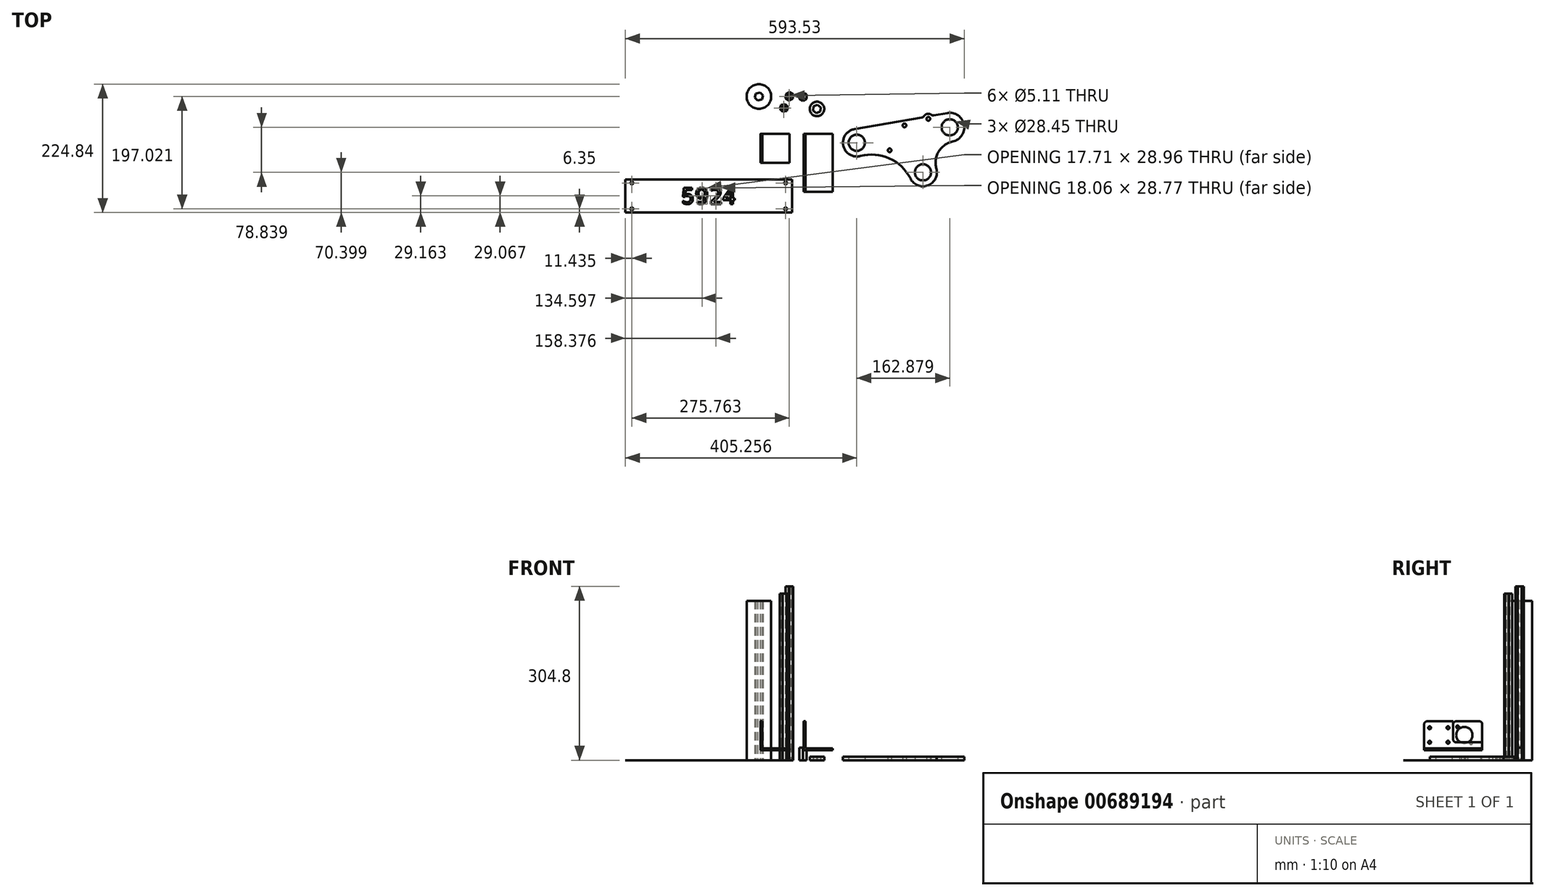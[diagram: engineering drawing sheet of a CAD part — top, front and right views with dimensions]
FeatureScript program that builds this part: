
annotation { "Feature Type Name" : "Feature", "Feature Type Description" : "" }
export const myFeature = defineFeature(function(context is Context, id is Id, definition is map)
    precondition{}
    {
        {
            var Q0;
            Q0=qCreatedBy(makeId("Front.planeOp"),FACE);
            var sketch = newSketch(context, id + "F0", { "sketchPlane" : qUnion([Q0])});
            skLineSegment(sketch, "E0", {"start": v(-58.96, 68.21) * mm, "end": v(-58.96, 17.41) * mm});
            skLineSegment(sketch, "E1", {"start": v(-58.96, 17.41) * mm, "end": v(-8.16, 17.41) * mm});
            skLineSegment(sketch, "E2", {"start": v(-8.16, 17.41) * mm, "end": v(-8.16, 20.59) * mm});
            skLineSegment(sketch, "E3", {"start": v(-8.16, 20.59) * mm, "end": v(-55.78, 20.59) * mm});
            skLineSegment(sketch, "E4", {"start": v(-55.78, 20.59) * mm, "end": v(-55.78, 68.21) * mm});
            skLineSegment(sketch, "E5", {"start": v(-55.78, 68.21) * mm, "end": v(-58.96, 68.21) * mm});
            skLineSegment(sketch, "E6", {"start": v(16.98, 68.21) * mm, "end": v(16.98, 17.41) * mm});
            skLineSegment(sketch, "E7", {"start": v(16.98, 17.41) * mm, "end": v(67.78, 17.41) * mm});
            skLineSegment(sketch, "E8", {"start": v(67.78, 17.41) * mm, "end": v(67.78, 20.59) * mm});
            skLineSegment(sketch, "E9", {"start": v(67.78, 20.59) * mm, "end": v(20.15, 20.59) * mm});
            skLineSegment(sketch, "E10", {"start": v(20.15, 20.59) * mm, "end": v(20.15, 68.21) * mm});
            skLineSegment(sketch, "E11", {"start": v(20.15, 68.21) * mm, "end": v(16.98, 68.21) * mm});
            skSolve(sketch);
        }
        {
            var Q0;
            Q0=makeQuery(id+"F0.imprint","IMPRINT",FACE,{"disambiguationData":[TD([[makeQuery(id+"F0.imprint","IMPRINT",EDGE,{"derivedFrom":sQuery(id+"F0.wireOp",EDGE,"E0")}),1.0]])]});
            extrude(context, id + "F1", {"entities" : qUnion([Q0]), "depth" : 50.8 * mm, "offsetDistance" : 25.4 * mm});
        }
        {
            var Q0;
            Q0=makeQuery(id+"F0.imprint","IMPRINT",FACE,{"disambiguationData":[TD([[makeQuery(id+"F0.imprint","IMPRINT",EDGE,{"derivedFrom":sQuery(id+"F0.wireOp",EDGE,"E6")}),1.0]])]});
            extrude(context, id + "F2", {"entities" : qUnion([Q0]), "depth" : 101.6 * mm, "offsetDistance" : 25.4 * mm});
        }
        {
            var Q0;
            Q0=makeQuery(id+"F1.opExtrude","SWEPT_FACE",FACE,{"disambiguationData":[OSD([sQuery(id+"F0.wireOp",EDGE,"E0")])]});
            var sketch = newSketch(context, id + "F3", { "sketchPlane" : qUnion([Q0])});
            skLineSegment(sketch, "E12.0.0", {"start": v(0, 68.21) * mm, "end": v(0, 17.41) * mm, "construction": true});
            skLineSegment(sketch, "E12.0.1", {"start": v(0, 17.41) * mm, "end": v(50.8, 17.41) * mm, "construction": true});
            skLineSegment(sketch, "E12.0.2", {"start": v(50.8, 17.41) * mm, "end": v(50.8, 68.21) * mm, "construction": true});
            skLineSegment(sketch, "E12.0.3", {"start": v(50.8, 68.21) * mm, "end": v(0, 68.21) * mm, "construction": true});
            skCircle(sketch, "E13", {"center": v(31.35, 44.08) * mm, "radius": 14.29 * mm});
            skCircle(sketch, "E14", {"center": v(31.35, 44.08) * mm, "radius": 15.56 * mm, "construction": true});
            skCircle(sketch, "E15", {"center": v(43.2, 58.26) * mm, "radius": 2.41 * mm});
            skCircle(sketch, "E16", {"center": v(19.5, 29.9) * mm, "radius": 2.41 * mm});
            skLineSegment(sketch, "E17", {"start": v(19.5, 29.9) * mm, "end": v(43.2, 58.26) * mm, "construction": true});
            skSolve(sketch);
        }
        {
            var Q0;
            Q0 = qSketchRegion(id + "F3", true);
            var Q1;
            Q1=makeQuery(id+"F1.opExtrude","SWEPT_FACE",FACE,{"disambiguationData":[OSD([sQuery(id+"F0.wireOp",EDGE,"E4")])]});
            extrude(context, id + "F4", {"entities" : qUnion([Q0]), "operationType" : NewBodyOperationType.REMOVE, "endBound" : BoundingType.UP_TO_SURFACE, "oppositeDirection" : true, "depth" : 25.4 * mm, "endBoundEntityFace" : qUnion([Q1]), "offsetDistance" : 25.4 * mm});
        }
        {
            var Q0;
            Q0=makeQuery(id+"F1.opExtrude","CAP_EDGE",EDGE,{"disambiguationData":[OSD([sQuery(id+"F0.wireOp",EDGE,"E5")])],"isStart":false});
            var Q1;
            Q1=makeQuery(id+"F1.opExtrude","CAP_EDGE",EDGE,{"disambiguationData":[OSD([sQuery(id+"F0.wireOp",EDGE,"E5")])],"isStart":true});
            fillet(context, id + "F5", {"entities" : qUnion([Q0, Q1]), "radius" : 5.08 * mm, "tangentPropagation" : true, "allowEdgeOverflow" : false});
        }
        {
            var Q0;
            Q0=makeQuery(id+"F2.opExtrude","SWEPT_FACE",FACE,{"disambiguationData":[OSD([sQuery(id+"F0.wireOp",EDGE,"E10")])]});
            var sketch = newSketch(context, id + "F6", { "sketchPlane" : qUnion([Q0])});
            skLineSegment(sketch, "E18.0.0", {"start": v(0, 20.59) * mm, "end": v(0, 68.21) * mm, "construction": true});
            skLineSegment(sketch, "E18.0.1", {"start": v(0, 68.21) * mm, "end": v(-101.6, 68.21) * mm, "construction": true});
            skLineSegment(sketch, "E18.0.2", {"start": v(-101.6, 68.21) * mm, "end": v(-101.6, 20.59) * mm, "construction": true});
            skLineSegment(sketch, "E18.0.3", {"start": v(-101.6, 20.59) * mm, "end": v(0, 20.59) * mm, "construction": true});
            skLineSegment(sketch, "E19.bottom", {"start": v(-92.08, 56.78) * mm, "end": v(-59.94, 56.78) * mm, "construction": true});
            skLineSegment(sketch, "E19.top", {"start": v(-92.08, 31.38) * mm, "end": v(-59.94, 31.38) * mm, "construction": true});
            skLineSegment(sketch, "E19.left", {"start": v(-92.08, 56.78) * mm, "end": v(-92.08, 31.38) * mm, "construction": true});
            skLineSegment(sketch, "E19.right", {"start": v(-59.94, 56.78) * mm, "end": v(-59.94, 31.38) * mm, "construction": true});
            skPoint(sketch, "E19.middle", {"position": v(-76, 44.08) * mm});
            skCircle(sketch, "E20", {"center": v(-92.08, 56.78) * mm, "radius": 2.55 * mm});
            skCircle(sketch, "E21", {"center": v(-92.08, 31.38) * mm, "radius": 2.55 * mm});
            skCircle(sketch, "E22", {"center": v(-59.94, 31.38) * mm, "radius": 2.55 * mm});
            skCircle(sketch, "E23", {"center": v(-59.94, 56.78) * mm, "radius": 2.55 * mm});
            skLineSegment(sketch, "E24.0", {"start": v(-101.6, 17.41) * mm, "end": v(0, 17.41) * mm, "construction": true});
            skLineSegment(sketch, "E25.bottom", {"start": v(0, 68.21) * mm, "end": v(-50.8, 68.21) * mm});
            skLineSegment(sketch, "E25.top", {"start": v(0, 31.38) * mm, "end": v(-50.8, 31.38) * mm});
            skLineSegment(sketch, "E25.left", {"start": v(0, 68.21) * mm, "end": v(0, 31.38) * mm});
            skLineSegment(sketch, "E25.right", {"start": v(-50.8, 68.21) * mm, "end": v(-50.8, 31.38) * mm});
            skSolve(sketch);
        }
        {
            var Q0;
            Q0 = qSketchRegion(id + "F6", true);
            var Q1;
            Q1=makeQuery(id+"F2.opExtrude","SWEPT_FACE",FACE,{"disambiguationData":[OSD([sQuery(id+"F0.wireOp",EDGE,"E6")])]});
            extrude(context, id + "F7", {"entities" : qUnion([Q0]), "operationType" : NewBodyOperationType.REMOVE, "endBound" : BoundingType.UP_TO_SURFACE, "oppositeDirection" : true, "depth" : 25.4 * mm, "endBoundEntityFace" : qUnion([Q1]), "offsetDistance" : 25.4 * mm});
        }
        {
            var Q0;
            Q0=makeQuery(id+"F7.boolean.opBoolean","COPY",EDGE,{"derivedFrom":makeQuery(id+"F7.opExtrude","SWEPT_EDGE",EDGE,{"disambiguationData":[OSD([sQuery(id+"F6.wireOp",EDGE,"E25.top"),sQuery(id+"F6.wireOp",EDGE,"E25.right")])]})});
            var Q1;
            Q1=makeQuery(id+"F7.boolean.opBoolean","COPY",EDGE,{"derivedFrom":makeQuery(id+"F7.opExtrude","SWEPT_EDGE",EDGE,{"disambiguationData":[OSD([sQuery(id+"F0.wireOp",EDGE,"E10"),sQuery(id+"F0.wireOp",EDGE,"E11"),sQuery(id+"F6.wireOp",EDGE,"E25.bottom"),sQuery(id+"F6.wireOp",EDGE,"E25.right")])]})});
            var Q2;
            Q2=makeQuery(id+"F2.opExtrude","CAP_EDGE",EDGE,{"disambiguationData":[OSD([sQuery(id+"F0.wireOp",EDGE,"E11")])],"isStart":false});
            var Q3;
            Q3=makeQuery(id+"F7.boolean.opBoolean","COPY",EDGE,{"derivedFrom":makeQuery(id+"F7.opExtrude","SWEPT_EDGE",EDGE,{"disambiguationData":[OSD([sQuery(id+"F0.wireOp",EDGE,"E10"),sQuery(id+"F6.wireOp",EDGE,"E25.top"),sQuery(id+"F6.wireOp",EDGE,"E25.left")])]})});
            fillet(context, id + "F8", {"entities" : qUnion([Q0, Q1, Q2, Q3]), "radius" : 5.08 * mm, "tangentPropagation" : true, "allowEdgeOverflow" : false});
        }
        {
            var Q0;
            Q0=qCreatedBy(makeId("Top.planeOp"),FACE);
            var sketch = newSketch(context, id + "F9", { "sketchPlane" : qUnion([Q0])});
            skCircle(sketch, "E26", {"center": v(-61.67, 65.53) * mm, "radius": 21.59 * mm});
            skCircle(sketch, "E27.cCircle", {"center": v(-61.67, 65.53) * mm, "radius": 6.35 * mm, "construction": true});
            skLineSegment(sketch, "E27.0", {"start": v(-56.54, 60.29) * mm, "end": v(-63.65, 58.47) * mm});
            skLineSegment(sketch, "E27.1", {"start": v(-63.65, 58.47) * mm, "end": v(-68.77, 63.71) * mm});
            skLineSegment(sketch, "E27.2", {"start": v(-68.77, 63.71) * mm, "end": v(-66.8, 70.77) * mm});
            skLineSegment(sketch, "E27.3", {"start": v(-66.8, 70.77) * mm, "end": v(-59.7, 72.59) * mm});
            skLineSegment(sketch, "E27.4", {"start": v(-59.7, 72.59) * mm, "end": v(-54.57, 67.35) * mm});
            skLineSegment(sketch, "E27.5", {"start": v(-54.57, 67.35) * mm, "end": v(-56.54, 60.29) * mm});
            skPoint(sketch, "E27.0.midPoint", {"position": v(-60.1, 59.38) * mm});
            skSolve(sketch);
        }
        {
            var Q0;
            Q0=makeQuery(id+"F9.imprint","IMPRINT",FACE,{"disambiguationData":[TD([[makeQuery(id+"F9.imprint","IMPRINT",EDGE,{"derivedFrom":sQuery(id+"F9.wireOp",EDGE,"E26")}),1.0]])]});
            extrude(context, id + "F10", {"entities" : qUnion([Q0]), "depth" : 279.4 * mm, "offsetDistance" : 25.4 * mm});
        }
        {
            var Q0;
            Q0=qCreatedBy(makeId("Top.planeOp"),FACE);
            var sketch = newSketch(context, id + "F11", { "sketchPlane" : qUnion([Q0])});
            skCircle(sketch, "E28", {"center": v(-8.38, 65.65) * mm, "radius": 2.55 * mm});
            skCircle(sketch, "E29.cCircle", {"center": v(-8.38, 65.65) * mm, "radius": 6.35 * mm, "construction": true});
            skLineSegment(sketch, "E29.0", {"start": v(-2.1, 61.88) * mm, "end": v(-8.5, 58.32) * mm});
            skLineSegment(sketch, "E29.1", {"start": v(-8.5, 58.32) * mm, "end": v(-14.8, 62.1) * mm});
            skLineSegment(sketch, "E29.2", {"start": v(-14.8, 62.1) * mm, "end": v(-14.67, 69.42) * mm});
            skLineSegment(sketch, "E29.3", {"start": v(-14.67, 69.42) * mm, "end": v(-8.26, 72.98) * mm});
            skLineSegment(sketch, "E29.4", {"start": v(-8.26, 72.98) * mm, "end": v(-1.97, 69.21) * mm});
            skLineSegment(sketch, "E29.5", {"start": v(-1.97, 69.21) * mm, "end": v(-2.1, 61.88) * mm});
            skPoint(sketch, "E29.0.midPoint", {"position": v(-5.3, 60.1) * mm});
            skSolve(sketch);
        }
        {
            var Q0;
            Q0=makeQuery(id+"F11.imprint","IMPRINT",FACE,{"disambiguationData":[TD([[makeQuery(id+"F11.imprint","IMPRINT",EDGE,{"derivedFrom":sQuery(id+"F11.wireOp",EDGE,"E28")}),-1.0]])]});
            extrude(context, id + "F12", {"entities" : qUnion([Q0]), "depth" : 304.8 * mm, "offsetDistance" : 25.4 * mm});
        }
        {
            var Q0;
            Q0=qCreatedBy(makeId("Top.planeOp"),FACE);
            var sketch = newSketch(context, id + "F13", { "sketchPlane" : qUnion([Q0])});
            skCircle(sketch, "E30.cCircle", {"center": v(15.3, 65.5) * mm, "radius": 6.35 * mm, "construction": true});
            skLineSegment(sketch, "E30.0", {"start": v(21.75, 62) * mm, "end": v(15.5, 58.17) * mm});
            skLineSegment(sketch, "E30.1", {"start": v(15.5, 58.17) * mm, "end": v(9.05, 61.67) * mm});
            skLineSegment(sketch, "E30.2", {"start": v(9.05, 61.67) * mm, "end": v(8.86, 69) * mm});
            skLineSegment(sketch, "E30.3", {"start": v(8.86, 69) * mm, "end": v(15.12, 72.83) * mm});
            skLineSegment(sketch, "E30.4", {"start": v(15.12, 72.83) * mm, "end": v(21.56, 69.32) * mm});
            skLineSegment(sketch, "E30.5", {"start": v(21.56, 69.32) * mm, "end": v(21.75, 62) * mm});
            skPoint(sketch, "E30.0.midPoint", {"position": v(18.62, 60.08) * mm});
            skSolve(sketch);
        }
        {
            var Q0;
            Q0=makeQuery(id+"F13.imprint","IMPRINT",FACE,{"disambiguationData":[TD([[makeQuery(id+"F13.imprint","IMPRINT",EDGE,{"derivedFrom":sQuery(id+"F13.wireOp",EDGE,"E30.0")}),-1.0]])]});
            extrude(context, id + "F14", {"entities" : qUnion([Q0]), "depth" : 22.22 * mm, "offsetDistance" : 25.4 * mm});
        }
        {
            var Q0;
            Q0=qCreatedBy(makeId("Top.planeOp"),FACE);
            var sketch = newSketch(context, id + "F15", { "sketchPlane" : qUnion([Q0])});
            skCircle(sketch, "E31", {"center": v(40.06, 43.79) * mm, "radius": 12.7 * mm});
            skCircle(sketch, "E32.cCircle", {"center": v(40.06, 43.79) * mm, "radius": 6.35 * mm, "construction": true});
            skLineSegment(sketch, "E32.0", {"start": v(45.92, 39.38) * mm, "end": v(39.17, 36.51) * mm});
            skLineSegment(sketch, "E32.1", {"start": v(39.17, 36.51) * mm, "end": v(33.31, 40.92) * mm});
            skLineSegment(sketch, "E32.2", {"start": v(33.31, 40.92) * mm, "end": v(34.2, 48.2) * mm});
            skLineSegment(sketch, "E32.3", {"start": v(34.2, 48.2) * mm, "end": v(40.95, 51.07) * mm});
            skLineSegment(sketch, "E32.4", {"start": v(40.95, 51.07) * mm, "end": v(46.8, 46.66) * mm});
            skLineSegment(sketch, "E32.5", {"start": v(46.8, 46.66) * mm, "end": v(45.92, 39.38) * mm});
            skPoint(sketch, "E32.0.midPoint", {"position": v(42.54, 37.95) * mm});
            skSolve(sketch);
        }
        {
            var Q0;
            Q0=makeQuery(id+"F15.imprint","IMPRINT",FACE,{"disambiguationData":[TD([[makeQuery(id+"F15.imprint","IMPRINT",EDGE,{"derivedFrom":sQuery(id+"F15.wireOp",EDGE,"E31")}),1.0]])]});
            extrude(context, id + "F16", {"entities" : qUnion([Q0]), "depth" : 6.35 * mm, "offsetDistance" : 25.4 * mm});
        }
        {
            var Q0;
            Q0=qCreatedBy(makeId("Top.planeOp"),FACE);
            var sketch = newSketch(context, id + "F17", { "sketchPlane" : qUnion([Q0])});
            skCircle(sketch, "E33", {"center": v(225.6, -67.32) * mm, "radius": 14.22 * mm});
            skArc(sketch, "E34", {"start": v(203.78, -78.25) * mm, "mid": v(234.39, -90.1) * mm, "end": v(249.13, -60.78) * mm});
            skCircle(sketch, "E35", {"center": v(272.55, 11.52) * mm, "radius": 14.22 * mm});
            skArc(sketch, "E36", {"start": v(277.87, -13.32) * mm, "mid": v(297.5, 16.35) * mm, "end": v(268.2, 36.54) * mm});
            skCircle(sketch, "E37", {"center": v(109.68, -15.47) * mm, "radius": 14.22 * mm});
            skArc(sketch, "E38", {"start": v(105.55, 8.3) * mm, "mid": v(86.11, -20.67) * mm, "end": v(115.92, -38.78) * mm});
            skArc(sketch, "E39", {"start": v(277.87, -13.32) * mm, "mid": v(253.25, -30.84) * mm, "end": v(249.13, -60.78) * mm});
            skLineSegment(sketch, "E40", {"start": v(268.2, 36.54) * mm, "end": v(241.95, 31.99) * mm});
            skArc(sketch, "E41", {"start": v(203.78, -78.25) * mm, "mid": v(166.88, -42.87) * mm, "end": v(115.92, -38.78) * mm});
            skCircle(sketch, "E42", {"center": v(225.6, -67.32) * mm, "radius": 21.59 * mm, "construction": true});
            skCircle(sketch, "E43", {"center": v(272.55, 11.52) * mm, "radius": 20.64 * mm, "construction": true});
            skCircle(sketch, "E44", {"center": v(167.29, -28.74) * mm, "radius": 3.24 * mm});
            skCircle(sketch, "E45", {"center": v(193.28, 14.9) * mm, "radius": 3.24 * mm});
            skLineSegment(sketch, "E46", {"start": v(193.28, 14.9) * mm, "end": v(167.29, -28.74) * mm, "construction": true});
            skLineSegment(sketch, "E47", {"start": v(272.55, 11.52) * mm, "end": v(225.6, -67.32) * mm, "construction": true});
            skArc(sketch, "E48", {"start": v(241.95, 31.99) * mm, "mid": v(233.48, 35.2) * mm, "end": v(226.6, 29.32) * mm});
            skCircle(sketch, "E49", {"center": v(235, 26.44) * mm, "radius": 3.24 * mm});
            skLineSegment(sketch, "E50.trimOffspring", {"start": v(226.6, 29.32) * mm, "end": v(105.55, 8.3) * mm});
            skSolve(sketch);
        }
        {
            var Q0;
            Q0=makeQuery(id+"F17.imprint","IMPRINT",FACE,{"disambiguationData":[TD([[makeQuery(id+"F17.imprint","IMPRINT",EDGE,{"derivedFrom":sQuery(id+"F17.wireOp",EDGE,"E33")}),-1.0]])]});
            extrude(context, id + "F18", {"entities" : qUnion([Q0]), "depth" : 6.35 * mm, "offsetDistance" : 25.4 * mm});
        }
        {
            var Q0;
            Q0=makeQuery(id+"F18.opExtrude","SWEPT_EDGE",EDGE,{"disambiguationData":[OSD([sQuery(id+"F17.wireOp",EDGE,"E48"),sQuery(id+"F17.wireOp",EDGE,"E50.trimOffspring")])]});
            var Q1;
            Q1=makeQuery(id+"F18.opExtrude","SWEPT_EDGE",EDGE,{"disambiguationData":[OSD([sQuery(id+"F17.wireOp",EDGE,"E40"),sQuery(id+"F17.wireOp",EDGE,"E48")])]});
            fillet(context, id + "F19", {"entities" : qUnion([Q0, Q1]), "radius" : 5.08 * mm, "tangentPropagation" : true, "allowEdgeOverflow" : false});
        }
        {
            var Q0;
            Q0=qCreatedBy(makeId("Top.planeOp"),FACE);
            var sketch = newSketch(context, id + "F20", { "sketchPlane" : qUnion([Q0])});
            skCircle(sketch, "E51.cCircle", {"center": v(-17.94, 45.55) * mm, "radius": 6.35 * mm, "construction": true});
            skLineSegment(sketch, "E51.0", {"start": v(-13.08, 40.06) * mm, "end": v(-20.26, 38.6) * mm});
            skLineSegment(sketch, "E51.1", {"start": v(-20.26, 38.6) * mm, "end": v(-25.12, 44.1) * mm});
            skLineSegment(sketch, "E51.2", {"start": v(-25.12, 44.1) * mm, "end": v(-22.8, 51.04) * mm});
            skLineSegment(sketch, "E51.3", {"start": v(-22.8, 51.04) * mm, "end": v(-15.61, 52.5) * mm});
            skLineSegment(sketch, "E51.4", {"start": v(-15.61, 52.5) * mm, "end": v(-10.75, 47.01) * mm});
            skLineSegment(sketch, "E51.5", {"start": v(-10.75, 47.01) * mm, "end": v(-13.08, 40.06) * mm});
            skPoint(sketch, "E51.0.midPoint", {"position": v(-16.67, 39.33) * mm});
            skCircle(sketch, "E52", {"center": v(-17.94, 45.55) * mm, "radius": 2.55 * mm});
            skSolve(sketch);
        }
        {
            var Q0;
            Q0=makeQuery(id+"F20.imprint","IMPRINT",FACE,{"disambiguationData":[TD([[makeQuery(id+"F20.imprint","IMPRINT",EDGE,{"derivedFrom":sQuery(id+"F20.wireOp",EDGE,"E51.0")}),-1.0]])]});
            extrude(context, id + "F21", {"entities" : qUnion([Q0]), "depth" : 292.1 * mm, "offsetDistance" : 25.4 * mm});
        }
        {
            var Q0;
            Q0=qCreatedBy(makeId("Top.planeOp"),FACE);
            var sketch = newSketch(context, id + "F22", { "sketchPlane" : qUnion([Q0])});
            skLineSegment(sketch, "E53.bottom", {"start": v(-295.58, -79.58) * mm, "end": v(-3.48, -79.58) * mm});
            skLineSegment(sketch, "E53.top", {"start": v(-295.58, -137.72) * mm, "end": v(-3.48, -137.72) * mm});
            skLineSegment(sketch, "E53.left", {"start": v(-295.58, -79.58) * mm, "end": v(-295.58, -137.72) * mm});
            skLineSegment(sketch, "E53.right", {"start": v(-3.48, -79.58) * mm, "end": v(-3.48, -137.72) * mm});
            skPoint(sketch, "E53.middle", {"position": v(-149.53, -108.65) * mm});
            skLineSegment(sketch, "E54.bottom", {"start": v(-284.15, -85.93) * mm, "end": v(-14.9, -85.93) * mm, "construction": true});
            skLineSegment(sketch, "E54.top", {"start": v(-284.15, -131.37) * mm, "end": v(-14.9, -131.37) * mm, "construction": true});
            skLineSegment(sketch, "E54.left", {"start": v(-284.15, -85.93) * mm, "end": v(-284.15, -131.37) * mm, "construction": true});
            skLineSegment(sketch, "E54.right", {"start": v(-14.9, -85.93) * mm, "end": v(-14.9, -131.37) * mm, "construction": true});
            skCircle(sketch, "E55", {"center": v(-284.15, -85.93) * mm, "radius": 2.55 * mm});
            skCircle(sketch, "E56", {"center": v(-284.15, -131.37) * mm, "radius": 2.55 * mm});
            skCircle(sketch, "E57", {"center": v(-14.9, -131.37) * mm, "radius": 2.55 * mm});
            skCircle(sketch, "E58", {"center": v(-14.9, -85.93) * mm, "radius": 2.55 * mm});
            skText(sketch, "E59", { "text": "5924\n", "fontName": "AllertaStencil-Regular.ttf"});
            const initialGuessF22  = {"E59": [-0.19775, -0.12294, 1, 0, 0.02858]};
            skSetInitialGuess(sketch, initialGuessF22);
            skSolve(sketch);
        }
        {
            var Q0;
            Q0=makeQuery(id+"F22.imprint","IMPRINT",FACE,{"disambiguationData":[TD([[makeQuery(id+"F22.imprint","IMPRINT",EDGE,{"derivedFrom":sQuery(id+"F22.wireOp",EDGE,"E53.bottom")}),-1.0]])]});
            extrude(context, id + "F23", {"entities" : qUnion([Q0]), "depth" : 1 / 203.2 * mm, "offsetDistance" : 25.4 * mm});
        }
    });
